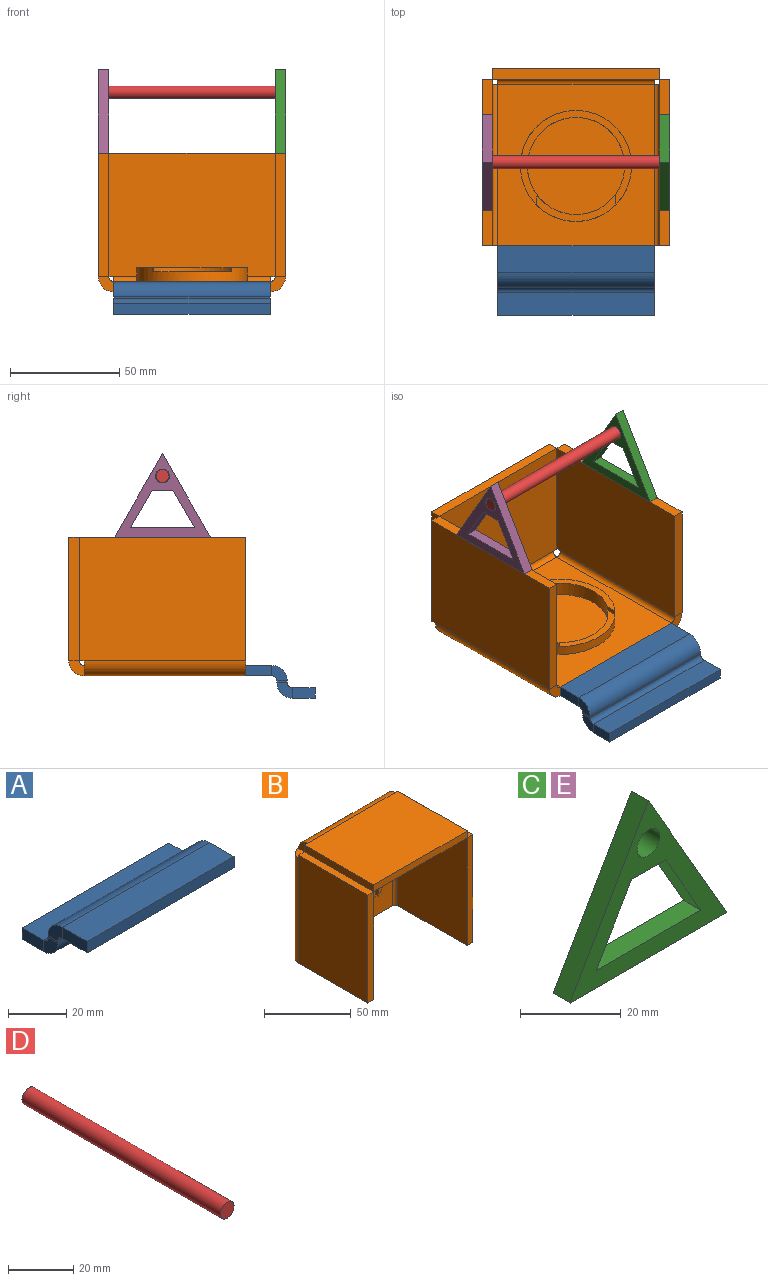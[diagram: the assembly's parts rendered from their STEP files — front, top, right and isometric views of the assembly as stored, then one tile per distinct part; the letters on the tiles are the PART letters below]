
ASSEMBLY  parts=5 mates=4
PART A: 22 faces, bbox 71.6x31.8x14.9 mm
  f0: plane 10.41x4.78mm, normal (-1,0,0), area 49.7mm2, adj f1,f3,f4,f19
  f1: plane 71.63x4.78mm, normal (0,1,0), area 342mm2, adj f0,f2,f3,f4
  f2: plane 10.41x4.78mm, normal (1,0,0), area 49.7mm2, adj f1,f3,f4,f18
  f3: plane 71.63x10.41mm, normal (0,0,-1), area 745.9mm2, adj f0,f1,f2,f20
  f4: plane 71.63x10.41mm, normal (0,0,1), area 745.9mm2, adj f0,f1,f2,f21
  f5: plane 4.78x0.81mm, normal (-1,0,0), area 3.9mm2, adj f7,f8,f14,f19
  f6: plane 4.78x0.81mm, normal (1,0,0), area 3.9mm2, adj f7,f8,f15,f18
  f7: plane 71.63x0.81mm, normal (0,-1,0), area 58.2mm2, adj f5,f6,f17,f20
  f8: plane 71.63x0.81mm, normal (0,1,0), area 58.2mm2, adj f5,f6,f16,f21
  f9: plane 71.63x4.78mm, normal (0,-1,0), area 342mm2, adj f10,f11,f12,f13
  f10: plane 11.99x4.78mm, normal (-1,0,0), area 57.2mm2, adj f9,f12,f13,f14
  f11: plane 11.99x4.78mm, normal (1,0,0), area 57.2mm2, adj f9,f12,f13,f15
  f12: plane 71.63x11.99mm, normal (0,0,-1), area 858.7mm2, adj f9,f10,f11,f17
  f13: plane 71.63x11.99mm, normal (0,0,1), area 858.7mm2, adj f9,f10,f11,f16
  f14: plane 7.06x7.06mm, normal (-1,0,0), area 35.1mm2, adj f5,f10,f16,f17
  f15: plane 7.06x7.06mm, normal (1,0,0), area 35.1mm2, adj f6,f11,f16,f17
  f16: cylinder r=7.06mm len=71.63mm, axis (-1,0,0), area 794.5mm2, adj f8,f13,f14,f15
  f17: cylinder r=2.29mm len=71.63mm, axis (-1,0,0), area 257.2mm2, adj f7,f12,f14,f15
  f18: plane 7.06x7.06mm, normal (1,0,0), area 35.1mm2, adj f2,f6,f20,f21
  f19: plane 7.06x7.06mm, normal (-1,0,0), area 35.1mm2, adj f0,f5,f20,f21
  f20: cylinder r=7.06mm len=71.63mm, axis (1,0,0), area 794.5mm2, adj f3,f7,f18,f19
  f21: cylinder r=2.29mm len=71.63mm, axis (1,0,0), area 257.2mm2, adj f4,f8,f18,f19
PART B: 41 faces, bbox 85.7x63.5x81 mm
  f0: cylinder r=22.23mm len=44.45mm, axis (0,1,0), area 807.2mm2, adj f36,f37,f38,f39,f40
  f1: plane 71.63x4.76mm, normal (0,0,-1), area 341.1mm2, adj f2,f3,f22,f32
  f2: plane 73.91x71.63mm, normal (0,1,0), area 5294.3mm2, adj f1,f13,f23,f33
  f3: plane 73.91x71.63mm, normal (0,-1,0), area 3267.5mm2, adj f1,f14,f24,f34,f35
  f4: plane 4.76x2.26mm, normal (0,1,0), area 10.8mm2, adj f6,f9,f10,f12
  f5: plane 76.15x4.76mm, normal (0,-1,0), area 362.7mm2, adj f6,f8,f9,f10
  f6: plane 56.45x4.76mm, normal (1,0,0), area 268.9mm2, adj f4,f5,f9,f10
  f7: plane 4.76x2.26mm, normal (0,1,0), area 10.8mm2, adj f8,f9,f10,f11
  f8: plane 56.45x4.76mm, normal (-1,0,0), area 268.9mm2, adj f5,f7,f9,f10
  f9: plane 76.15x56.45mm, normal (0,0,1), area 4298.7mm2, adj f4,f5,f6,f7,f8,f13
  f10: plane 76.15x56.45mm, normal (0,0,-1), area 4298.7mm2, adj f4,f5,f6,f7,f8,f14
  f11: plane 7.05x7.05mm, normal (-1,0,0), area 34.9mm2, adj f7,f13,f14,f31
  f12: plane 7.05x7.05mm, normal (1,0,0), area 34.9mm2, adj f4,f13,f14,f21
  f13: cylinder r=7.05mm len=71.63mm, axis (-1,0,0), area 793mm2, adj f2,f9,f11,f12
  f14: cylinder r=2.29mm len=71.63mm, axis (-1,0,0), area 257.2mm2, adj f3,f10,f11,f12
  f15: plane 76.17x4.76mm, normal (0,-1,0), area 362.8mm2, adj f16,f18,f19,f20
  f16: plane 56.45x4.76mm, normal (0,0,-1), area 268.9mm2, adj f15,f19,f20,f22
  f17: plane 4.76x2.26mm, normal (0,1,0), area 10.8mm2, adj f18,f19,f20,f21
  f18: plane 56.45x4.76mm, normal (0,0,1), area 268.9mm2, adj f15,f17,f19,f20
  f19: plane 76.17x56.45mm, normal (1,0,0), area 4300.2mm2, adj f15,f16,f17,f18,f23
  f20: plane 76.17x56.45mm, normal (-1,0,0), area 4300.2mm2, adj f15,f16,f17,f18,f24
  f21: plane 7.05x7.05mm, normal (0,0,1), area 34.9mm2, adj f12,f17,f23,f24
  f22: plane 7.05x7.05mm, normal (0,0,-1), area 34.9mm2, adj f1,f16,f23,f24
  f23: cylinder r=7.05mm len=73.91mm, axis (0,0,1), area 818.4mm2, adj f2,f19,f21,f22
  f24: cylinder r=2.29mm len=73.91mm, axis (0,0,1), area 265.4mm2, adj f3,f20,f21,f22
  f25: plane 4.76x2.26mm, normal (0,1,0), area 10.8mm2, adj f27,f29,f30,f31
  f26: plane 76.17x4.76mm, normal (0,-1,0), area 362.8mm2, adj f27,f28,f29,f30
  f27: plane 56.45x4.76mm, normal (0,0,1), area 268.9mm2, adj f25,f26,f29,f30
  f28: plane 56.45x4.76mm, normal (0,0,-1), area 268.9mm2, adj f26,f29,f30,f32
  f29: plane 76.17x56.45mm, normal (-1,0,0), area 4300.2mm2, adj f25,f26,f27,f28,f33
  f30: plane 76.17x56.45mm, normal (1,0,0), area 4300.2mm2, adj f25,f26,f27,f28,f34
  f31: plane 7.05x7.05mm, normal (0,0,1), area 34.9mm2, adj f11,f25,f33,f34
  f32: plane 7.05x7.05mm, normal (0,0,-1), area 34.9mm2, adj f1,f28,f33,f34
  f33: cylinder r=7.05mm len=73.91mm, axis (0,0,1), area 818.4mm2, adj f2,f29,f31,f32
  f34: cylinder r=2.29mm len=73.91mm, axis (0,0,1), area 265.4mm2, adj f3,f30,f31,f32
  f35: cylinder r=25.4mm len=50.8mm, axis (0,1,0), area 936.9mm2, adj f3,f36,f38,f39,f40
  f36: plane 50.8x43.27mm, normal (0,-1,0), area 345.3mm2, adj f0,f35,f38,f39
  f37: plane 44.45x44.45mm, normal (0,-1,0), area 1551.8mm2, adj f0
  f38: plane 4.6x1.91mm, normal (1,0,-0.05), area 8.8mm2, adj f0,f35,f36,f40
  f39: plane 4.9x1.91mm, normal (-1,0,0), area 9.3mm2, adj f0,f35,f36,f40
  f40: plane 36.1x12.43mm, normal (0,-1,0), area 129.7mm2, adj f0,f35,f38,f39
PART C: 10 faces, bbox 44x4.8x38.1 mm
  f0: plane 38.1x22mm, normal (-0.87,0,0.5), area 210.1mm2, adj f1,f7,f8,f9
  f1: plane 43.99x4.78mm, normal (0,0,-1), area 210.1mm2, adj f0,f7,f8,f9
  f2: plane 29.33x4.78mm, normal (0,0,1), area 140.1mm2, adj f3,f5,f8,f9
  f3: plane 17.14x9.9mm, normal (0.87,0,-0.5), area 94.5mm2, adj f2,f4,f8,f9
  f4: plane 9.54x4.78mm, normal (0,0,-1), area 45.5mm2, adj f3,f5,f8,f9
  f5: plane 17.14x9.9mm, normal (-0.87,0,-0.5), area 94.5mm2, adj f2,f4,f8,f9
  f6: cylinder r=3.17mm len=6.35mm, axis (0,1,0), area 95.3mm2, adj f8,f9
  f7: plane 38.1x22mm, normal (0.87,0,0.5), area 210.1mm2, adj f0,f1,f8,f9
  f8: plane 43.99x38.1mm, normal (0,-1,0), area 473.3mm2, adj f0,f1,f2,f3,f4,f5,f6,f7
  f9: plane 43.99x38.1mm, normal (0,1,0), area 473.3mm2, adj f0,f1,f2,f3,f4,f5,f6,f7
PART D: 3 faces, bbox 6x85.8x6 mm
  f0: cylinder r=2.98mm len=85.75mm, axis (0,1,0), area 1608mm2, adj f1,f2
  f1: plane 5.97x5.97mm, normal (0,-1,0), area 28mm2, adj f0
  f2: plane 5.97x5.97mm, normal (0,1,0), area 28mm2, adj f0
PART E: same geometry as C
PLACE A rot(axis=(0,0,-1),180deg) t=(-43.22,-127.02,-50.5)mm
PLACE B rot(axis=(-1,0,0),90deg) t=(-64.81,-78.47,-40.33)mm
PLACE C rot(axis=(0,0,-1),90deg) t=(-21.94,-78.49,35.87)mm
PLACE D rot(axis=(0,0,1),90deg) t=(-107.69,-78.49,51.11)mm
PLACE E rot(axis=(0,0,-1),90deg) t=(-102.9,-78.49,35.87)mm
MATE fastened A.f9 <-> B.f1  axis (0,1,0) through (-64.81,-116.57,-37.95)mm
MATE fastened D.f0 <-> C.f6  axis (1,0,0) through (-21.94,-78.49,51.11)mm
MATE fastened C.f1 <-> B.f15  axis (0,0,-1) through (-24.33,-78.49,23.17)mm
MATE fastened E.f1 <-> B.f26  axis (0,0,-1) through (-105.29,-78.49,23.17)mm
